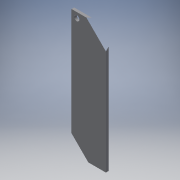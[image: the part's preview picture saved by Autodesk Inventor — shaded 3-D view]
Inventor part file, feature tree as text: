
AUTODESK INVENTOR PART (.ipt)
format: ipt  version: 2016 (Build 200138000, 138)  size: 103,936 bytes
history: native  units: mm
features: extrude x2, sketch x2, other x1
ambient origin geometry x8: Origin, YZ Plane, XZ Plane, XY Plane, X Axis, Y Axis, Z Axis, Center Point
bodies: Body1 (feature_tree)
feature tree (5):
  other  "ソリッド1"
  extrude  "押し出し1"  Depth=13.0mm
  extrude  "押し出し2"  Depth=47.0mm
  sketch  "スケッチ1"
  sketch  "スケッチ2"
